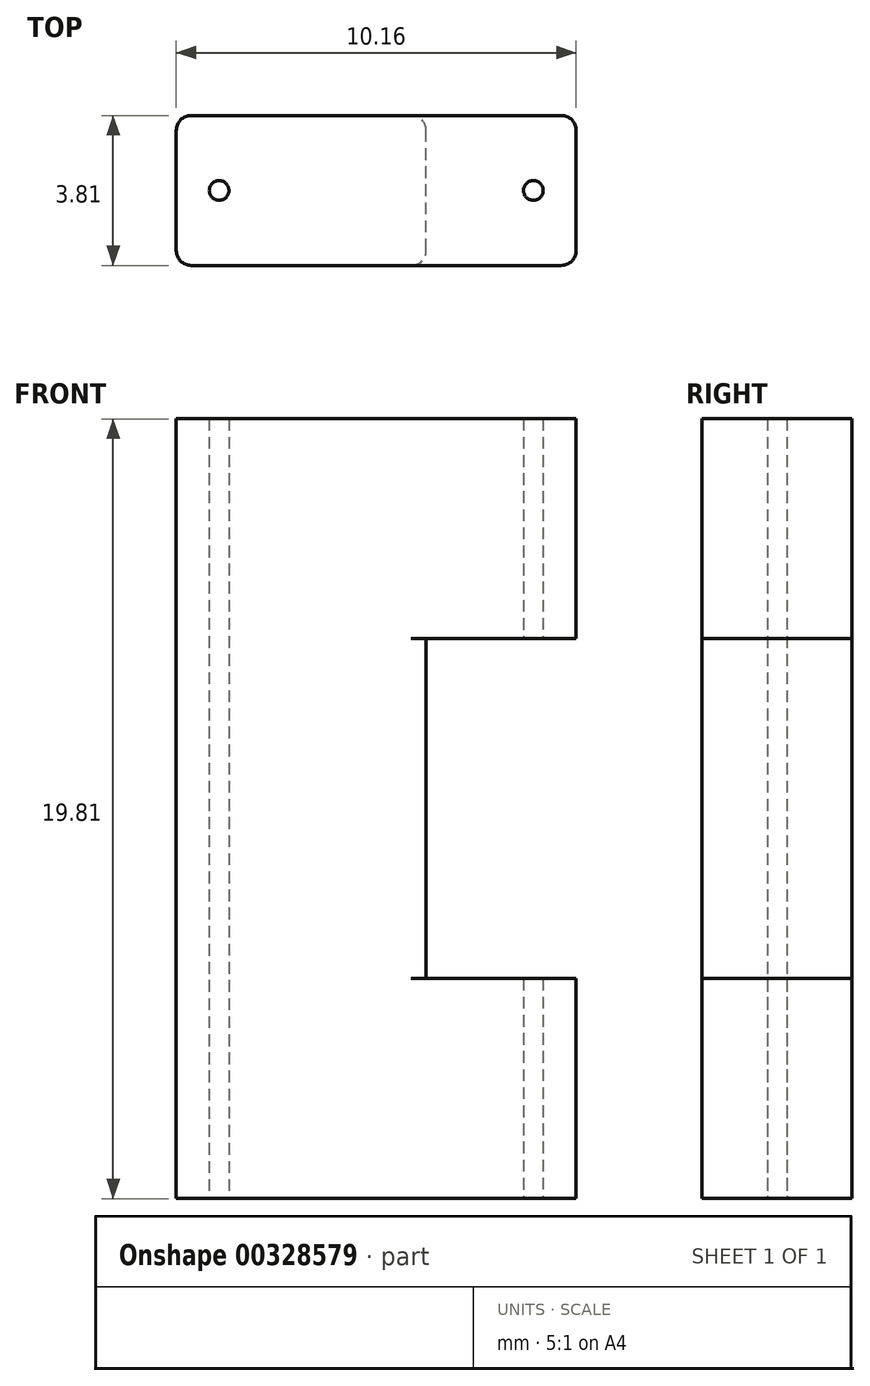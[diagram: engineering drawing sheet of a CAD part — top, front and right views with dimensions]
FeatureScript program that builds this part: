
annotation { "Feature Type Name" : "Feature", "Feature Type Description" : "" }
export const myFeature = defineFeature(function(context is Context, id is Id, definition is map)
    precondition{}
    {
        {
            var Q0;
            Q0=qCreatedBy(makeId("Front.planeOp"),FACE);
            var sketch = newSketch(context, id + "F0", { "sketchPlane" : qUnion([Q0])});
            skLineSegment(sketch, "E0.bottom", {"start": v(17.02, -29.15) * mm, "end": v(27.18, -29.15) * mm});
            skLineSegment(sketch, "E0.top", {"start": v(17.02, -48.96) * mm, "end": v(27.18, -48.96) * mm});
            skLineSegment(sketch, "E0.left", {"start": v(17.02, -29.15) * mm, "end": v(17.02, -34.73) * mm});
            skLineSegment(sketch, "E0.right", {"start": v(27.18, -29.15) * mm, "end": v(27.18, -34.73) * mm});
            skLineSegment(sketch, "E1", {"start": v(17.02, -48.96) * mm, "end": v(23.37, -48.96) * mm});
            skLineSegment(sketch, "E2", {"start": v(23.37, -43.37) * mm, "end": v(23.37, -34.73) * mm});
            skLineSegment(sketch, "E3", {"start": v(27.18, -34.73) * mm, "end": v(23.37, -34.73) * mm});
            skLineSegment(sketch, "E4", {"start": v(27.18, -48.96) * mm, "end": v(27.18, -43.37) * mm});
            skLineSegment(sketch, "E5", {"start": v(27.18, -43.37) * mm, "end": v(23.37, -43.37) * mm});
            skLineSegment(sketch, "E6.trimOffspring", {"start": v(27.18, -43.37) * mm, "end": v(27.18, -48.96) * mm});
            skLineSegment(sketch, "E7.trimOffspring", {"start": v(17.02, -43.37) * mm, "end": v(17.02, -48.96) * mm});
            skLineSegment(sketch, "E8", {"start": v(17.02, -43.37) * mm, "end": v(23.37, -43.37) * mm});
            skLineSegment(sketch, "E9", {"start": v(23.37, -34.73) * mm, "end": v(17.02, -34.73) * mm});
            skLineSegment(sketch, "E10", {"start": v(17.02, -34.73) * mm, "end": v(17.02, -43.37) * mm});
            skPoint(sketch, "E11.start.orphan", {"position": v(13.21, -34.73) * mm});
            skSolve(sketch);
        }
        {
            var Q0;
            Q0=makeQuery(id+"F0.imprint","IMPRINT",FACE,{"disambiguationData":[TD([[makeQuery(id+"F0.imprint","IMPRINT",EDGE,{"derivedFrom":sQuery(id+"F0.wireOp",EDGE,"E2")}),1.0]])]});
            extrude(context, id + "F1", {"entities" : qUnion([Q0]), "depth" : 3.8 * mm});
        }
        {
            var Q0;
            Q0=makeQuery(id+"F1.opExtrude","CAP_FACE",FACE,{"disambiguationData":[OSD([sQuery(id+"F0.wireOp",EDGE,"E2"),sQuery(id+"F0.wireOp",EDGE,"kWP5FoFF-B6KL-BZVV-yxeF-1pJlTzE3f1qg"),sQuery(id+"F0.wireOp",EDGE,"NCTPWaSt-j8r5-npNt-1snH-QZKrF3ifEW0c"),sQuery(id+"F0.wireOp",EDGE,"E11"),sQuery(id+"F0.wireOp",EDGE,"E8"),sQuery(id+"F0.wireOp",EDGE,"E9")])],"isStart":false});
            var sketch = newSketch(context, id + "F2", { "sketchPlane" : qUnion([Q0])});
            skLineSegment(sketch, "E12.bottom", {"start": v(17.02, -29.15) * mm, "end": v(27.18, -29.15) * mm});
            skLineSegment(sketch, "E12.left", {"start": v(17.02, -29.15) * mm, "end": v(17.02, -34.73) * mm});
            skLineSegment(sketch, "E13", {"start": v(27.18, -29.15) * mm, "end": v(27.18, -34.73) * mm});
            skLineSegment(sketch, "E14", {"start": v(27.18, -34.73) * mm, "end": v(23.37, -34.73) * mm});
            skLineSegment(sketch, "E15", {"start": v(23.37, -34.73) * mm, "end": v(17.02, -34.73) * mm});
            skLineSegment(sketch, "E16.MirrorCS", {"start": v(23.37, -43.37) * mm, "end": v(17.02, -43.37) * mm});
            skLineSegment(sketch, "E17.MirrorCS", {"start": v(27.18, -43.37) * mm, "end": v(23.37, -43.37) * mm});
            skLineSegment(sketch, "E18.MirrorCS", {"start": v(27.18, -48.96) * mm, "end": v(27.18, -43.37) * mm});
            skLineSegment(sketch, "E19.MirrorCS", {"start": v(17.02, -48.96) * mm, "end": v(17.02, -43.37) * mm});
            skLineSegment(sketch, "E20.MirrorCS", {"start": v(17.02, -48.96) * mm, "end": v(27.18, -48.96) * mm});
            skSolve(sketch);
        }
        {
            var Q0;
            Q0=qSketchRegion(id+"F2",true);
            extrude(context, id + "F3", {"entities" : qUnion([Q0]), "operationType" : NewBodyOperationType.ADD, "oppositeDirection" : true, "depth" : 3.81 * mm, "hasSecondDirection" : true, "secondDirectionOppositeDirection" : true, "secondDirectionDepth" : 0 * mm});
        }
        {
            var Q0;
            Q0=makeQuery(id+"F3.opExtrude","SWEPT_FACE",FACE,{"disambiguationData":[OSD([sQuery(id+"F2.wireOp",EDGE,"E20.MirrorCS")])]});
            var sketch = newSketch(context, id + "F4", { "sketchPlane" : qUnion([Q0])});
            skCircle(sketch, "E21", {"center": v(26.1, 1.9) * mm, "radius": 0.25 * mm});
            skLineSegment(sketch, "E22", {"start": v(22.1, 0) * mm, "end": v(22.1, 3.8) * mm});
            skCircle(sketch, "E23.MirrorC", {"center": v(18.11, 1.9) * mm, "radius": 0.25 * mm});
            skSolve(sketch);
        }
        {
            var Q0;
            Q0=qSketchRegion(id+"F4",true);
            extrude(context, id + "F5", {"entities" : qUnion([Q0]), "operationType" : NewBodyOperationType.REMOVE, "oppositeDirection" : true, "depth" : 50.8 * mm});
        }
        {
            var Q0;
            Q0=makeQuery(id+"F3.opExtrude","CAP_EDGE",EDGE,{"disambiguationData":[OSD([sQuery(id+"F2.wireOp",EDGE,"E13")])],"isStart":true});
            var Q1;
            Q1=makeQuery(id+"F3.opExtrude","CAP_EDGE",EDGE,{"disambiguationData":[OSD([sQuery(id+"F2.wireOp",EDGE,"E12.left")])],"isStart":true});
            var Q2;
            Q2=makeQuery(id+"F3.opExtrude","CAP_EDGE",EDGE,{"disambiguationData":[OSD([sQuery(id+"F2.wireOp",EDGE,"E18.MirrorCS")])],"isStart":true});
            var Q3;
            Q3=makeQuery(id+"F3.opExtrude","CAP_EDGE",EDGE,{"disambiguationData":[OSD([sQuery(id+"F2.wireOp",EDGE,"E19.MirrorCS")])],"isStart":true});
            var Q4;
            Q4=makeQuery(id+"F1.opExtrude","CAP_EDGE",EDGE,{"disambiguationData":[OSD([sQuery(id+"F0.wireOp",EDGE,"E2")])],"isStart":false});
            var Q5;
            Q5=makeQuery(id+"F1.opExtrude","CAP_EDGE",EDGE,{"disambiguationData":[OSD([sQuery(id+"F0.wireOp",EDGE,"NCTPWaSt-j8r5-npNt-1snH-QZKrF3ifEW0c")])],"isStart":false});
            var Q6;
            Q6=makeQuery(id+"F1.opExtrude","CAP_EDGE",EDGE,{"disambiguationData":[OSD([sQuery(id+"F0.wireOp",EDGE,"E2")])],"isStart":true});
            var Q7;
            Q7=makeQuery(id+"F1.opExtrude","CAP_EDGE",EDGE,{"disambiguationData":[OSD([sQuery(id+"F0.wireOp",EDGE,"NCTPWaSt-j8r5-npNt-1snH-QZKrF3ifEW0c")])],"isStart":true});
            var Q8;
            Q8=makeQuery(id+"F3.opExtrude","CAP_EDGE",EDGE,{"disambiguationData":[OSD([sQuery(id+"F2.wireOp",EDGE,"E12.left")])],"isStart":false});
            var Q9;
            Q9=makeQuery(id+"F3.opExtrude","CAP_EDGE",EDGE,{"disambiguationData":[OSD([sQuery(id+"F2.wireOp",EDGE,"E13")])],"isStart":false});
            var Q10;
            Q10=makeQuery(id+"F3.opExtrude","CAP_EDGE",EDGE,{"disambiguationData":[OSD([sQuery(id+"F2.wireOp",EDGE,"E18.MirrorCS")])],"isStart":false});
            var Q11;
            Q11=makeQuery(id+"F3.opExtrude","CAP_EDGE",EDGE,{"disambiguationData":[OSD([sQuery(id+"F2.wireOp",EDGE,"E19.MirrorCS")])],"isStart":false});
            var Q12;
            Q12=makeQuery(id+"F3.boolean.opBoolean","MERGE",EDGE,{"derivedFrom":[makeQuery(id+"F1.opExtrude","CAP_EDGE",EDGE,{"disambiguationData":[OSD([sQuery(id+"F0.wireOp",EDGE,"E11"),sQuery(id+"F0.wireOp",EDGE,"E9")])],"isStart":false}),makeQuery(id+"F3.opExtrude","CAP_EDGE",EDGE,{"disambiguationData":[OSD([sQuery(id+"F2.wireOp",EDGE,"E14"),sQuery(id+"F2.wireOp",EDGE,"E15")])],"isStart":true})]});
            fillet(context, id + "F6", {"entities" : qUnion([Q0, Q1, Q2, Q3, Q4, Q5, Q6, Q7, Q8, Q9, Q10, Q11, Q12]), "radius" : 0.38 * mm, "tangentPropagation" : true, "allowEdgeOverflow" : false});
        }
    });
